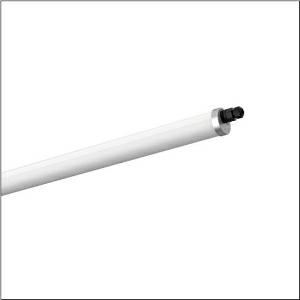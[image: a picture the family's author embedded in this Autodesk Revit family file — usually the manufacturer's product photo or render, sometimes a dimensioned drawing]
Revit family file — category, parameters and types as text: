
# Revit family: monsun_r__31_tube_51ft107n480a_b45d
name_source: partatom
category: Lighting Fixtures
units: mm (PartAtom-declared; Revit-internal decimal feet)

## family parameters
Cut with Voids When Loaded = No
Host = Face
Light Source = No
Part Type = Normal
Room Calculation Point = No
Round Connector Dimension = Use Diameter
Shared = No

## types (1)
- Monsun® 31 Tube (1 x LED, 8000 lm, 50 W, 4000K)
    Apparent Load = 50 VA
    CIE Flux Codes = 42 71 89 91 100
    Color Rendering = 80
    Color Temperature = 4000K
    Default Elevation = 1800 mm
    Description = Monsun® 31 Tube, tubular luminaire, primary optical cover: diffuser, of PMMA, light emission: direct distribution, primary light characteristic: symmetric, installation type: suspended mounting, surface-mounted, LED, rated luminous flux: 8.000lm, luminous efficacy: 160lm/W, light colour: 840, colour temperature: 4000K, with with 1 terminal, 3-pole, max. 2.5mm², through-wiring: 3x 1.5mm², mains connection: 220..240V, AC, 50/60Hz, rated input power: 50W, housing, cylindrical, of PMMA, semi-transparent, matt white, length: 1.560mm, diameter: 75mm, end cap, of stainless steel (V2A), protection rating (complete): IP67/IP69K, insulation class (complete): insulation class I (protective earthing), certification: CE, UKCA, impact resistance: IK07, permissible operating ambient temperature: -20..+40°C, corresponds to IFS (International Featured Standards) requirements for safety and quality in the food industry, packaging unit: 1 piece
    Height = 83 mm
    Lamp = 1 x LED
    Lamp Light Flux = 8000 lm
    Lamp Power = 50 W
    Lamp count = 1
    Length = 1560 mm
    Luminous efficacy = 160 lm/W
    Manufacturer = Siteco
    ModVariant = No
    Model = 51FT107N480A
    Mounting Place = Ceiling
    Mounting Type = Pendant
    Number of Poles = 1
    OnlyDefault = Yes
    Power Factor = 1
    Product Name = Monsun® 31 Tube
    Product group = tubular luminaire
    ProductGroupID = 907
    Protection Class = Protection class I
    RLX_Detail_Level = 1
    RlxData = <blob elided: 24873 chars, md5=d233380b>
    Socket = socket
    Standby Power = 0 W
    System Light Flux = 8000 lm
    System Power = 50 W
    Type Comments = Product without accessories
    Type Image = l_1228461.jpg
    URL = http://relux.com
    VarID = ---
    Voltage = 0 V
    Weight = 0.00 kg
    Width = 75 mm

## geometry (parser evidence)
native form markers: Blend x4, Sweep x12
no freeform markers — native parametric forms only
